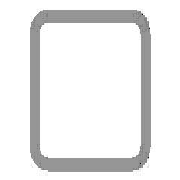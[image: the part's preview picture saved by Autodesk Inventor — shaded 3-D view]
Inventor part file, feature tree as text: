
AUTODESK INVENTOR PART (.ipt)
format: ipt  version: 2024 (Build 280153000, 153)  size: 128,512 bytes
history: native  units: mm (DEFAULTED — no unit token found)
features: other x4, extrude x1, sketch x1, plane x1
ambient origin geometry x8: Origin, YZ Plane, XZ Plane, XY Plane, X Axis, Y Axis, Z Axis, Center Point
bodies: Solid1 (feature_tree)
feature tree (7):
  parser-record x1  (decoder bookkeeping rows leaked as tree rows — omitted from the tree; the rows remain in map.json)
  other  "Driven Length"
  other  "Plano inicial"
  other  "Plano final"
  extrude  "Cuerpo"  TaperAngle=0.0deg  [1 undecoded]
  sketch  "Sketch3"  dims[d3=1890.0mm d4=0.0mm d10=50.8mm d11=50.8mm d12=3.175mm d13=-0.0mm d14=1890.0mm d15=25.4mm d16=25.4mm d17=6.35mm d18=90.0deg d19=1890.0mm]
  plane  "Work Plane3"
note: 1 required parameter value undecoded (feature->parameter linkage not recoverable at this tier; creation-order binding heuristic only, values carry confidence <= 0.55)
